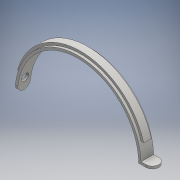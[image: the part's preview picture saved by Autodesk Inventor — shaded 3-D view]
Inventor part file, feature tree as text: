
AUTODESK INVENTOR PART (.ipt)
format: ipt  version: 2016 (Build 200138000, 138)  size: 169,472 bytes
history: native  units: mm
features: extrude x5, sketch x5, plane x2
ambient origin geometry x8: Origin, YZ Plane, XZ Plane, XY Plane, X Axis, Y Axis, Z Axis, Center Point
bodies: Solid1 (feature_tree)
feature tree (12):
  extrude  "Extrusion1"  Depth=5.0mm TaperAngle=0.0deg
  extrude  "Extrusion2"  Depth=3.0mm TaperAngle=0.0deg
  plane  "Work Plane1"
  extrude  "Extrusion3"  Depth=3.0mm
  extrude  "Extrusion4"  Depth=2.5mm
  plane  "Work Plane2"
  extrude  "Extrusion5"  Depth=3.0mm TaperAngle=0.0deg
  sketch  "Sketch1"  dims[d4=5.0mm d5=0.0mm d7=5.0mm d8=0.0mm]
  sketch  "Sketch2"  dims[d9=-25.0mm d13=3.0mm d14=0.0mm]
  sketch  "Sketch3"  dims[d15=4.5mm d16=3.0mm]
  sketch  "Sketch4"  dims[d17=4.0mm d18=0.0mm d21=2.5mm]
  sketch  "Sketch6"  dims[d22=52.0mm d23=7.0mm d24=3.0mm d25=0.0mm]
